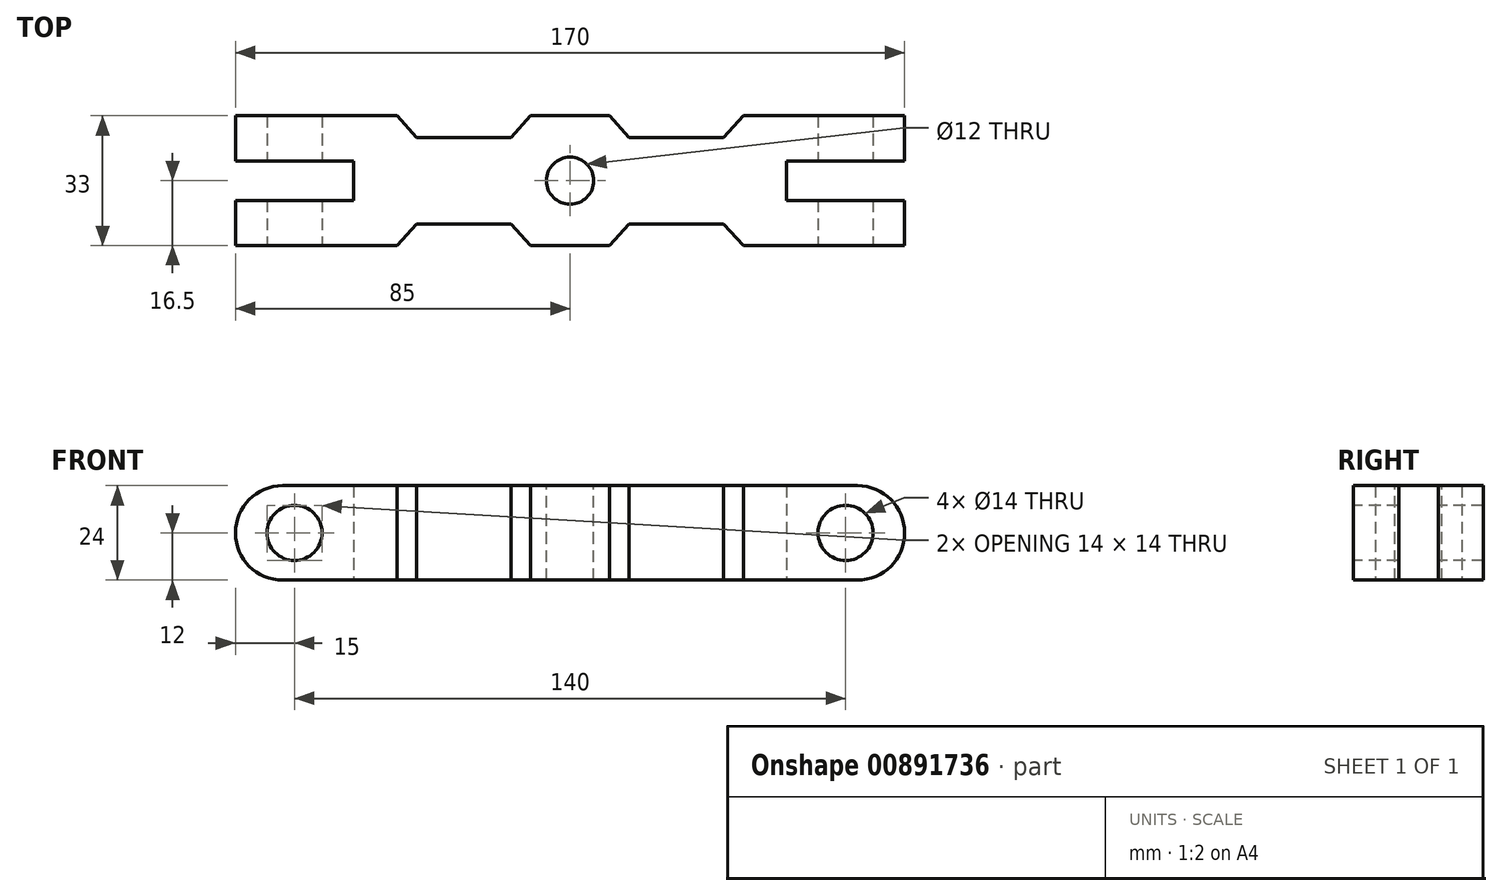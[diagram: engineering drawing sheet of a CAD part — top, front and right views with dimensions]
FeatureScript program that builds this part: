
annotation { "Feature Type Name" : "Feature", "Feature Type Description" : "" }
export const myFeature = defineFeature(function(context is Context, id is Id, definition is map)
    precondition{}
    {
        {
            var Q0;
            Q0=qCreatedBy(makeId("Top.planeOp"),FACE);
            var sketch = newSketch(context, id + "F0", { "sketchPlane" : qUnion([Q0])});
            skLineSegment(sketch, "E0", {"start": v(0, 16.5) * mm, "end": v(10, 16.5) * mm});
            skLineSegment(sketch, "E1", {"start": v(10, 16.5) * mm, "end": v(15, 11) * mm});
            skLineSegment(sketch, "E2", {"start": v(15, 11) * mm, "end": v(39, 11) * mm});
            skLineSegment(sketch, "E3", {"start": v(39, 11) * mm, "end": v(44, 16.5) * mm});
            skLineSegment(sketch, "E4", {"start": v(44, 16.5) * mm, "end": v(85, 16.5) * mm});
            skLineSegment(sketch, "E5", {"start": v(85, 16.5) * mm, "end": v(85, 5) * mm});
            skLineSegment(sketch, "E6", {"start": v(85, 5) * mm, "end": v(55, 5) * mm});
            skLineSegment(sketch, "E7", {"start": v(55, 5) * mm, "end": v(55, 0) * mm});
            skLineSegment(sketch, "E8.MirrorCS", {"start": v(85, -5) * mm, "end": v(55, -5) * mm});
            skLineSegment(sketch, "E9.MirrorCS", {"start": v(39, -11) * mm, "end": v(44, -16.5) * mm});
            skLineSegment(sketch, "E10.MirrorCS", {"start": v(15, -11) * mm, "end": v(39, -11) * mm});
            skLineSegment(sketch, "E11.MirrorCS", {"start": v(0, -16.5) * mm, "end": v(10, -16.5) * mm});
            skLineSegment(sketch, "E12.MirrorCS", {"start": v(55, -5) * mm, "end": v(55, 0) * mm});
            skLineSegment(sketch, "E13.MirrorCS", {"start": v(44, -16.5) * mm, "end": v(85, -16.5) * mm});
            skLineSegment(sketch, "E14.MirrorCS", {"start": v(85, -16.5) * mm, "end": v(85, -5) * mm});
            skLineSegment(sketch, "E15.MirrorCS", {"start": v(10, -16.5) * mm, "end": v(15, -11) * mm});
            skLineSegment(sketch, "E16.MirrorCS", {"start": v(-44, -16.5) * mm, "end": v(-85, -16.5) * mm});
            skLineSegment(sketch, "E17.MirrorCS", {"start": v(-85, 16.5) * mm, "end": v(-85, 5) * mm});
            skLineSegment(sketch, "E18.MirrorCS", {"start": v(-85, -5) * mm, "end": v(-55, -5) * mm});
            skLineSegment(sketch, "E19.MirrorCS", {"start": v(-55, 5) * mm, "end": v(-55, 0) * mm});
            skLineSegment(sketch, "E20.MirrorCS", {"start": v(-85, 5) * mm, "end": v(-55, 5) * mm});
            skLineSegment(sketch, "E21.MirrorCS", {"start": v(-44, 16.5) * mm, "end": v(-85, 16.5) * mm});
            skLineSegment(sketch, "E22.MirrorCS", {"start": v(-15, 11) * mm, "end": v(-39, 11) * mm});
            skLineSegment(sketch, "E23.MirrorCS", {"start": v(-10, -16.5) * mm, "end": v(-15, -11) * mm});
            skLineSegment(sketch, "E24.MirrorCS", {"start": v(0, 16.5) * mm, "end": v(-10, 16.5) * mm});
            skLineSegment(sketch, "E25.MirrorCS", {"start": v(-39, 11) * mm, "end": v(-44, 16.5) * mm});
            skLineSegment(sketch, "E26.MirrorCS", {"start": v(0, -16.5) * mm, "end": v(-10, -16.5) * mm});
            skLineSegment(sketch, "E27.MirrorCS", {"start": v(-39, -11) * mm, "end": v(-44, -16.5) * mm});
            skLineSegment(sketch, "E28.MirrorCS", {"start": v(-15, -11) * mm, "end": v(-39, -11) * mm});
            skLineSegment(sketch, "E29.MirrorCS", {"start": v(-85, -16.5) * mm, "end": v(-85, -5) * mm});
            skLineSegment(sketch, "E30.MirrorCS", {"start": v(-10, 16.5) * mm, "end": v(-15, 11) * mm});
            skLineSegment(sketch, "E31.MirrorCS", {"start": v(-55, -5) * mm, "end": v(-55, 0) * mm});
            skSolve(sketch);
        }
        {
            var Q0;
            Q0 = qSketchRegion(id + "F0", true);
            extrude(context, id + "F1", {"entities" : qUnion([Q0]), "endBound" : BoundingType.SYMMETRIC, "depth" : 24 * mm, "offsetDistance" : 25 * mm});
        }
        {
            var Q0;
            Q0=qCreatedBy(makeId("Top.planeOp"),FACE);
            var sketch = newSketch(context, id + "F2", { "sketchPlane" : qUnion([Q0])});
            skCircle(sketch, "E32", {"center": v(0, 0) * mm, "radius": 6 * mm});
            skSolve(sketch);
        }
        {
            var Q0;
            Q0 = qSketchRegion(id + "F2", true);
            extrude(context, id + "F3", {"entities" : qUnion([Q0]), "operationType" : NewBodyOperationType.REMOVE, "endBound" : BoundingType.SYMMETRIC, "oppositeDirection" : true, "depth" : 50 * mm, "offsetDistance" : 25 * mm});
        }
        {
            var Q0;
            Q0=qCreatedBy(makeId("Front.planeOp"),FACE);
            var sketch = newSketch(context, id + "F4", { "sketchPlane" : qUnion([Q0])});
            skCircle(sketch, "E33", {"center": v(70, 0) * mm, "radius": 7 * mm});
            skCircle(sketch, "E34.MirrorC", {"center": v(-70, 0) * mm, "radius": 7 * mm});
            skSolve(sketch);
        }
        {
            var Q0;
            Q0 = qSketchRegion(id + "F4", true);
            extrude(context, id + "F5", {"entities" : qUnion([Q0]), "operationType" : NewBodyOperationType.REMOVE, "endBound" : BoundingType.SYMMETRIC, "oppositeDirection" : true, "depth" : 100 * mm, "offsetDistance" : 25 * mm});
        }
        {
            var Q0;
            Q0=makeQuery(id+"F1.opExtrude","CAP_EDGE",EDGE,{"disambiguationData":[OSD([sQuery(id+"F0.wireOp",EDGE,"E5")])],"isStart":false});
            var Q1;
            Q1=makeQuery(id+"F1.opExtrude","CAP_EDGE",EDGE,{"disambiguationData":[OSD([sQuery(id+"F0.wireOp",EDGE,"E14.MirrorCS")])],"isStart":false});
            var Q2;
            Q2=makeQuery(id+"F1.opExtrude","CAP_EDGE",EDGE,{"disambiguationData":[OSD([sQuery(id+"F0.wireOp",EDGE,"E14.MirrorCS")])],"isStart":true});
            var Q3;
            Q3=makeQuery(id+"F1.opExtrude","CAP_EDGE",EDGE,{"disambiguationData":[OSD([sQuery(id+"F0.wireOp",EDGE,"E5")])],"isStart":true});
            fillet(context, id + "F6", {"entities" : qUnion([Q0, Q1, Q2, Q3]), "radius" : 12 * mm, "tangentPropagation" : true, "allowEdgeOverflow" : false});
        }
        {
            var Q0;
            Q0=makeQuery(id+"F1.opExtrude","CAP_EDGE",EDGE,{"disambiguationData":[OSD([sQuery(id+"F0.wireOp",EDGE,"E29.MirrorCS")])],"isStart":false});
            var Q1;
            Q1=makeQuery(id+"F1.opExtrude","CAP_EDGE",EDGE,{"disambiguationData":[OSD([sQuery(id+"F0.wireOp",EDGE,"E17.MirrorCS")])],"isStart":false});
            var Q2;
            Q2=makeQuery(id+"F1.opExtrude","CAP_EDGE",EDGE,{"disambiguationData":[OSD([sQuery(id+"F0.wireOp",EDGE,"E17.MirrorCS")])],"isStart":true});
            var Q3;
            Q3=makeQuery(id+"F1.opExtrude","CAP_EDGE",EDGE,{"disambiguationData":[OSD([sQuery(id+"F0.wireOp",EDGE,"E29.MirrorCS")])],"isStart":true});
            fillet(context, id + "F7", {"entities" : qUnion([Q0, Q1, Q2, Q3]), "radius" : 12 * mm, "tangentPropagation" : true, "allowEdgeOverflow" : false});
        }
    });
